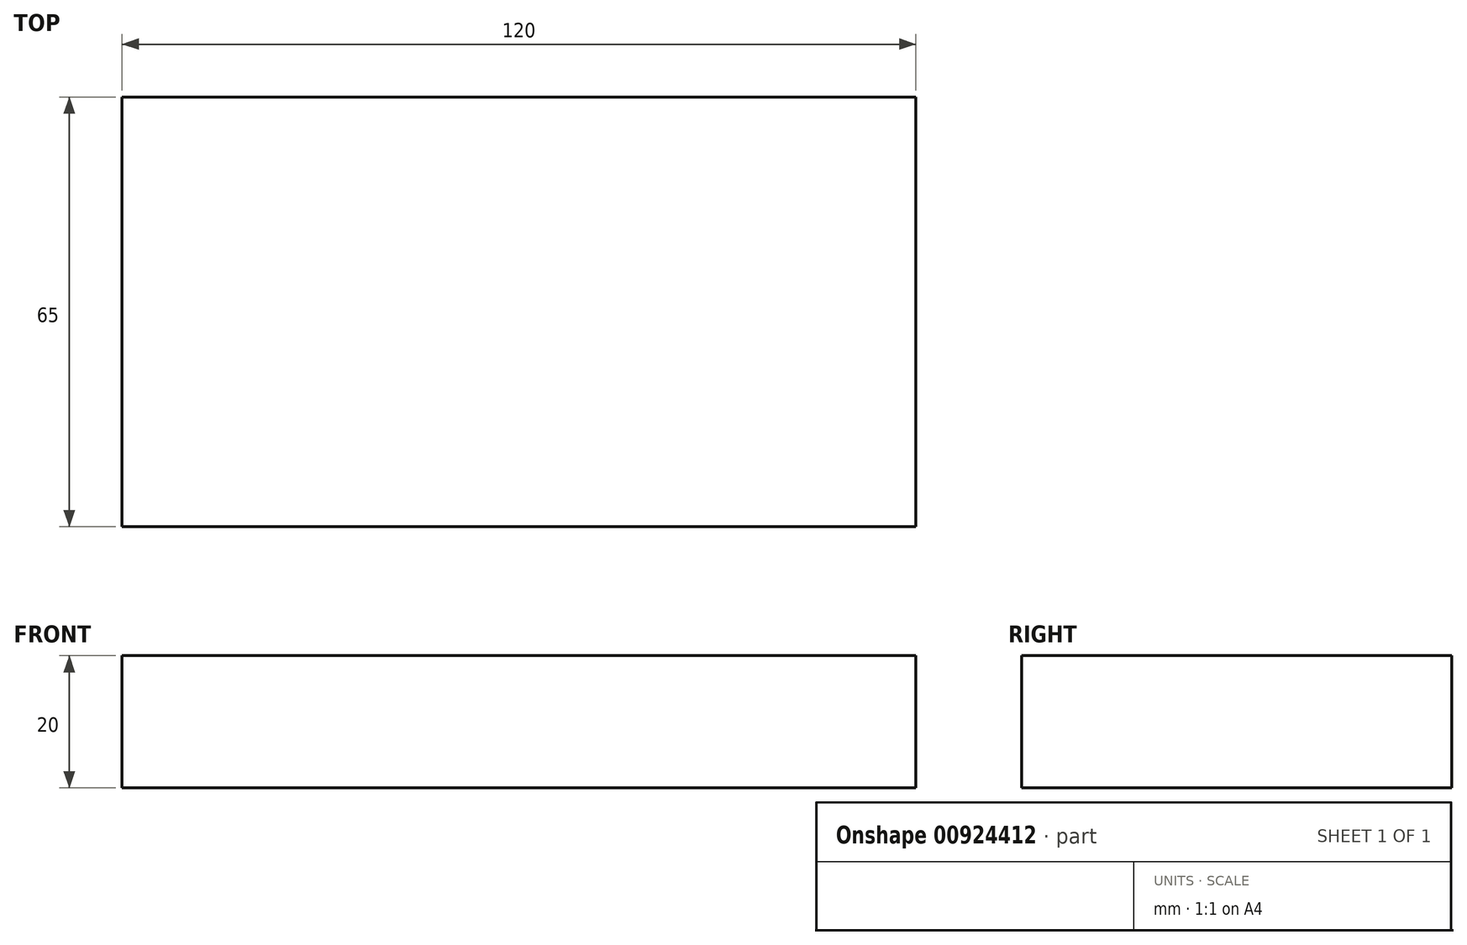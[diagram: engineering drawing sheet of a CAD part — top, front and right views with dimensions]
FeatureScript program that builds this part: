
annotation { "Feature Type Name" : "Feature", "Feature Type Description" : "" }
export const myFeature = defineFeature(function(context is Context, id is Id, definition is map)
    precondition{}
    {
        {
            var Q0;
            Q0=qCreatedBy(makeId("Top.planeOp"),FACE);
            var sketch = newSketch(context, id + "F0", { "sketchPlane" : qUnion([Q0])});
            skLineSegment(sketch, "E0.bottom", {"start": v(0, 0) * mm, "end": v(120, 0) * mm});
            skLineSegment(sketch, "E0.top", {"start": v(0, 65) * mm, "end": v(120, 65) * mm});
            skLineSegment(sketch, "E0.left", {"start": v(0, 0) * mm, "end": v(0, 65) * mm});
            skLineSegment(sketch, "E0.right", {"start": v(120, 0) * mm, "end": v(120, 65) * mm});
            skSolve(sketch);
        }
        {
            var Q0;
            Q0 = qSketchRegion(id + "F0", true);
            extrude(context, id + "F1", {"entities" : qUnion([Q0]), "depth" : 20 * mm, "offsetDistance" : 25 * mm});
        }
    });
